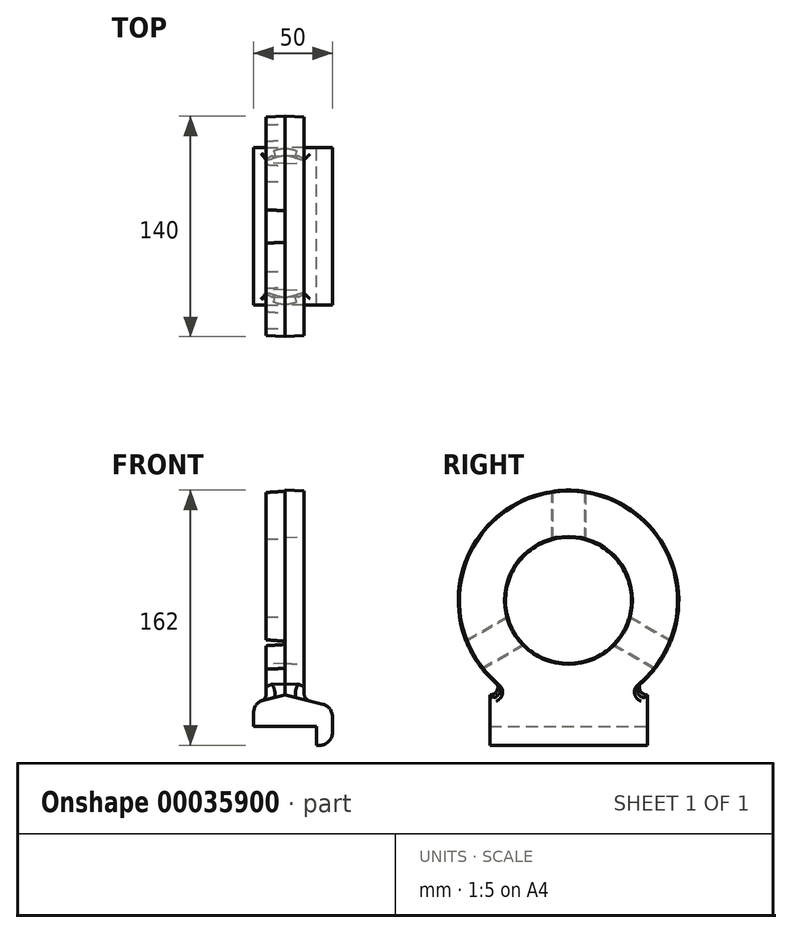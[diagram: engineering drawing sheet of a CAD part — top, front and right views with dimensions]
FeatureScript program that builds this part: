
annotation { "Feature Type Name" : "Feature", "Feature Type Description" : "" }
export const myFeature = defineFeature(function(context is Context, id is Id, definition is map)
    precondition{}
    {
        {
            var Q0;
            Q0=qCreatedBy(makeId("Right.planeOp"),FACE);
            var sketch = newSketch(context, id + "F0", { "sketchPlane" : qUnion([Q0])});
            skLineSegment(sketch, "E0", {"start": v(0, 0) * mm, "end": v(0, -80) * mm});
            skLineSegment(sketch, "E1", {"start": v(0, -80) * mm, "end": v(-49.5, -80) * mm});
            skArc(sketch, "E2", {"start": v(45.15, -53.5) * mm, "mid": v(0, 70) * mm, "end": v(-45.15, -53.5) * mm});
            skCircle(sketch, "E3", {"center": v(0, 0) * mm, "radius": 40 * mm});
            skLineSegment(sketch, "E4", {"start": v(0, 0) * mm, "end": v(-10, 0) * mm});
            skLineSegment(sketch, "E5", {"start": v(-10, 38.73) * mm, "end": v(-10, 69.28) * mm});
            skLineSegment(sketch, "E6", {"start": v(-10, 69.28) * mm, "end": v(-10, 78.9) * mm});
            skLineSegment(sketch, "E7.MirrorCS", {"start": v(10, 38.73) * mm, "end": v(10, 69.28) * mm});
            skLineSegment(sketch, "E8.2.1", {"start": v(-5, -8.66) * mm, "end": v(0, -11.55) * mm});
            skLineSegment(sketch, "E9", {"start": v(-49.5, -80) * mm, "end": v(-42.68, -68.98) * mm});
            skLineSegment(sketch, "E10.MirrorCS", {"start": v(49.5, -80) * mm, "end": v(42.68, -68.98) * mm});
            skLineSegment(sketch, "E11.MirrorCS", {"start": v(0, -80) * mm, "end": v(49.5, -80) * mm});
            skPoint(sketch, "E12.visualSharp", {"position": v(-36.83, -59.53) * mm});
            skArc(sketch, "E12.filletArc", {"start": v(-42.68, -68.98) * mm, "mid": v(-41.04, -60.78) * mm, "end": v(-45.15, -53.5) * mm});
            skPoint(sketch, "E13.visualSharp", {"position": v(36.83, -59.53) * mm});
            skArc(sketch, "E13.filletArc", {"start": v(45.15, -53.5) * mm, "mid": v(41.04, -60.78) * mm, "end": v(42.68, -68.98) * mm});
            skLineSegment(sketch, "E14.trimOffspring", {"start": v(-28.54, -28.03) * mm, "end": v(-55, -43.3) * mm});
            skLineSegment(sketch, "E15.trimOffspring", {"start": v(-38.54, -10.7) * mm, "end": v(-65, -25.98) * mm});
            skLineSegment(sketch, "E16.trimOffspring", {"start": v(38.54, -10.7) * mm, "end": v(65, -25.98) * mm});
            skLineSegment(sketch, "E17.trimOffspring", {"start": v(28.54, -28.03) * mm, "end": v(55, -43.3) * mm});
            skPoint(sketch, "E18.orphan", {"position": v(10, 0) * mm});
            skSolve(sketch);
        }
        {
            var Q0;
            {var subQ1=sQuery(id+"F0.wireOp",EDGE,"E5");Q0=makeQuery(id+"F0.imprint","IMPRINT",FACE,{"disambiguationData":[TD([[makeQuery(id+"F0.imprint","IMPRINT",EDGE,{"derivedFrom":subQ1}),1.0]])]});}
            var Q1;
            {var subQ6=sQuery(id+"F0.wireOp",EDGE,"E1");Q1=makeQuery(id+"F0.imprint","IMPRINT",FACE,{"disambiguationData":[TD([[makeQuery(id+"F0.imprint","IMPRINT",EDGE,{"derivedFrom":subQ6}),-1.0]])]});}
            var Q2;
            Q2=makeQuery(id+"F0.imprint","IMPRINT",FACE,{"disambiguationData":[TD([[makeQuery(id+"F0.imprint","IMPRINT",EDGE,{"derivedFrom":sQuery(id+"F0.wireOp",EDGE,"E10.MirrorCS")}),1.0]])]});
            var Q3;
            {var subQ1=sQuery(id+"F0.wireOp",EDGE,"E16.trimOffspring");Q3=makeQuery(id+"F0.imprint","IMPRINT",FACE,{"disambiguationData":[TD([[makeQuery(id+"F0.imprint","IMPRINT",EDGE,{"derivedFrom":subQ1}),-1.0]])]});}
            var Q4;
            {var subQ1=sQuery(id+"F0.wireOp",EDGE,"E7.MirrorCS");Q4=makeQuery(id+"F0.imprint","IMPRINT",FACE,{"disambiguationData":[TD([[makeQuery(id+"F0.imprint","IMPRINT",EDGE,{"derivedFrom":subQ1}),-1.0]])]});}
            var Q5;
            {var subQ1=sQuery(id+"F0.wireOp",EDGE,"E14.trimOffspring");Q5=makeQuery(id+"F0.imprint","IMPRINT",FACE,{"disambiguationData":[TD([[makeQuery(id+"F0.imprint","IMPRINT",EDGE,{"derivedFrom":subQ1}),-1.0]])]});}
            var Q6;
            {var subQ1=sQuery(id+"F0.wireOp",EDGE,"E5");Q6=makeQuery(id+"F0.imprint","IMPRINT",FACE,{"disambiguationData":[TD([[makeQuery(id+"F0.imprint","IMPRINT",EDGE,{"derivedFrom":subQ1}),-1.0]])]});}
            extrude(context, id + "F1", {"entities" : qUnion([Q0, Q1, Q2, Q3, Q4, Q5, Q6]), "depth" : 12 * mm, "hasDraft" : true, "draftAngle" : 3 * degree, "draftPullDirection" : true});
        }
        {
            var Q0;
            {var subQ1=sQuery(id+"F0.wireOp",EDGE,"E7.MirrorCS");Q0=makeQuery(id+"F0.imprint","IMPRINT",FACE,{"disambiguationData":[TD([[makeQuery(id+"F0.imprint","IMPRINT",EDGE,{"derivedFrom":subQ1}),-1.0]])]});}
            var Q1;
            Q1=makeQuery(id+"F0.imprint","IMPRINT",FACE,{"disambiguationData":[TD([[makeQuery(id+"F0.imprint","IMPRINT",EDGE,{"derivedFrom":sQuery(id+"F0.wireOp",EDGE,"E10.MirrorCS")}),1.0]])]});
            var Q2;
            {var subQ6=sQuery(id+"F0.wireOp",EDGE,"E1");Q2=makeQuery(id+"F0.imprint","IMPRINT",FACE,{"disambiguationData":[TD([[makeQuery(id+"F0.imprint","IMPRINT",EDGE,{"derivedFrom":subQ6}),-1.0]])]});}
            var Q3;
            {var subQ1=sQuery(id+"F0.wireOp",EDGE,"E5");Q3=makeQuery(id+"F0.imprint","IMPRINT",FACE,{"disambiguationData":[TD([[makeQuery(id+"F0.imprint","IMPRINT",EDGE,{"derivedFrom":subQ1}),1.0]])]});}
            extrude(context, id + "F2", {"entities" : qUnion([Q0, Q1, Q2, Q3]), "operationType" : NewBodyOperationType.ADD, "oppositeDirection" : true, "depth" : 12 * mm, "hasDraft" : true, "draftAngle" : 3 * degree, "draftPullDirection" : true});
        }
        {
            var Q0;
            Q0=qCreatedBy(makeId("Front.planeOp"),FACE);
            var sketch = newSketch(context, id + "F3", { "sketchPlane" : qUnion([Q0])});
            skLineSegment(sketch, "E19", {"start": v(-20, -80) * mm, "end": v(20, -80) * mm});
            skLineSegment(sketch, "E20", {"start": v(13.94, -63.49) * mm, "end": v(0, -60) * mm});
            skPoint(sketch, "E21.end.orphan", {"position": v(-30, 0) * mm});
            skPoint(sketch, "E22.visualSharp", {"position": v(20, -65) * mm});
            skLineSegment(sketch, "E23.MirrorCS", {"start": v(22, -92) * mm, "end": v(20, -92) * mm});
            skLineSegment(sketch, "E24.MirrorCS", {"start": v(-20, -80) * mm, "end": v(-20, -71.25) * mm});
            skLineSegment(sketch, "E25.MirrorCS", {"start": v(20, -92) * mm, "end": v(20, -80) * mm});
            skLineSegment(sketch, "E26.MirrorCS", {"start": v(30, -73.75) * mm, "end": v(30, -84) * mm});
            skArc(sketch, "E27.MirrorCS", {"start": v(23.94, -65.99) * mm, "mid": v(28.3, -68.82) * mm, "end": v(30, -73.75) * mm});
            skArc(sketch, "E28.MirrorCS", {"start": v(-20, -71.25) * mm, "mid": v(-18.3, -66.32) * mm, "end": v(-13.94, -63.49) * mm});
            skArc(sketch, "E29.MirrorCS", {"start": v(30, -84) * mm, "mid": v(27.66, -89.66) * mm, "end": v(22, -92) * mm});
            skLineSegment(sketch, "E30.MirrorCS", {"start": v(23.94, -65.99) * mm, "end": v(0, -60) * mm});
            skLineSegment(sketch, "E31.MirrorCS", {"start": v(20, -80) * mm, "end": v(-20, -80) * mm});
            skLineSegment(sketch, "E32.MirrorCS", {"start": v(-13.94, -63.49) * mm, "end": v(0, -60) * mm});
            skPoint(sketch, "E33.MirrorP", {"position": v(-20, -65) * mm});
            skSolve(sketch);
        }
        {
            var Q0;
            Q0=makeQuery(id+"F3.imprint","IMPRINT",FACE,{"disambiguationData":[TD([[makeQuery(id+"F3.imprint","IMPRINT",EDGE,{"derivedFrom":sQuery(id+"F3.wireOp",EDGE,"E23.MirrorCS")}),-1.0]])]});
            extrude(context, id + "F4", {"entities" : qUnion([Q0]), "operationType" : NewBodyOperationType.ADD, "depth" : 50 * mm, "hasSecondDirection" : true, "secondDirectionOppositeDirection" : true, "secondDirectionDepth" : 50 * mm});
        }
        {
            var Q0;
            Q0=makeQuery(id+"F4.boolean.opBoolean","INTERSECT",EDGE,{"derivedFrom":[makeQuery(id+"F1.opExtrude","CAP_FACE",FACE,{"disambiguationData":[OSD([sQuery(id+"F0.wireOp",EDGE,"E1"),sQuery(id+"F0.wireOp",EDGE,"E2"),sQuery(id+"F0.wireOp",EDGE,"E3"),sQuery(id+"F0.wireOp",EDGE,"E9"),sQuery(id+"F0.wireOp",EDGE,"E10.MirrorCS"),sQuery(id+"F0.wireOp",EDGE,"E11.MirrorCS"),sQuery(id+"F0.wireOp",EDGE,"E12.filletArc"),sQuery(id+"F0.wireOp",EDGE,"E13.filletArc")])],"isStart":false}),makeQuery(id+"F4.opExtrude","SWEPT_FACE",FACE,{"disambiguationData":[OSD([sQuery(id+"F3.wireOp",EDGE,"E30.MirrorCS")])]})]});
            fillet(context, id + "F5", {"entities" : qUnion([Q0]), "radius" : 5 * mm, "tangentPropagation" : true, "allowEdgeOverflow" : false});
        }
        {
            var Q0;
            Q0=makeQuery(id+"F4.boolean.opBoolean","INTERSECT",EDGE,{"derivedFrom":[makeQuery(id+"F2.opExtrude","CAP_FACE",FACE,{"disambiguationData":[OSD([sQuery(id+"F0.wireOp",EDGE,"E1"),sQuery(id+"F0.wireOp",EDGE,"E2"),sQuery(id+"F0.wireOp",EDGE,"E3"),sQuery(id+"F0.wireOp",EDGE,"E9"),sQuery(id+"F0.wireOp",EDGE,"E10.MirrorCS"),sQuery(id+"F0.wireOp",EDGE,"E11.MirrorCS"),sQuery(id+"F0.wireOp",EDGE,"E12.filletArc"),sQuery(id+"F0.wireOp",EDGE,"E13.filletArc"),sQuery(id+"F0.wireOp",EDGE,"E14.trimOffspring"),sQuery(id+"F0.wireOp",EDGE,"E17.trimOffspring")])],"isStart":false}),makeQuery(id+"F4.opExtrude","SWEPT_FACE",FACE,{"disambiguationData":[OSD([sQuery(id+"F3.wireOp",EDGE,"E32.MirrorCS")])]})]});
            var Q1;
            Q1=makeQuery(id+"F4.boolean.opBoolean","INTERSECT",EDGE,{"derivedFrom":[makeQuery(id+"F2.opExtrude","SWEPT_FACE",FACE,{"disambiguationData":[OSD([sQuery(id+"F0.wireOp",EDGE,"E12.filletArc")])]}),makeQuery(id+"F4.opExtrude","SWEPT_FACE",FACE,{"disambiguationData":[OSD([sQuery(id+"F3.wireOp",EDGE,"E32.MirrorCS")])]})]});
            var Q2;
            Q2=makeQuery(id+"F4.boolean.opBoolean","INTERSECT",EDGE,{"derivedFrom":[makeQuery(id+"F1.opExtrude","SWEPT_FACE",FACE,{"disambiguationData":[OSD([sQuery(id+"F0.wireOp",EDGE,"E12.filletArc")])]}),makeQuery(id+"F4.opExtrude","SWEPT_FACE",FACE,{"disambiguationData":[OSD([sQuery(id+"F3.wireOp",EDGE,"E30.MirrorCS")])]})]});
            var Q3;
            Q3=makeQuery(id+"F4.boolean.opBoolean","INTERSECT",EDGE,{"derivedFrom":[makeQuery(id+"F2.opExtrude","SWEPT_FACE",FACE,{"disambiguationData":[OSD([sQuery(id+"F0.wireOp",EDGE,"E13.filletArc")])]}),makeQuery(id+"F4.opExtrude","SWEPT_FACE",FACE,{"disambiguationData":[OSD([sQuery(id+"F3.wireOp",EDGE,"E32.MirrorCS")])]})]});
            var Q4;
            Q4=makeQuery(id+"F4.boolean.opBoolean","INTERSECT",EDGE,{"derivedFrom":[makeQuery(id+"F1.opExtrude","SWEPT_FACE",FACE,{"disambiguationData":[OSD([sQuery(id+"F0.wireOp",EDGE,"E13.filletArc")])]}),makeQuery(id+"F4.opExtrude","SWEPT_FACE",FACE,{"disambiguationData":[OSD([sQuery(id+"F3.wireOp",EDGE,"E30.MirrorCS")])]})]});
            fillet(context, id + "F6", {"entities" : qUnion([Q0, Q1, Q2, Q3, Q4]), "radius" : 5 * mm, "tangentPropagation" : true, "allowEdgeOverflow" : false});
        }
    });
